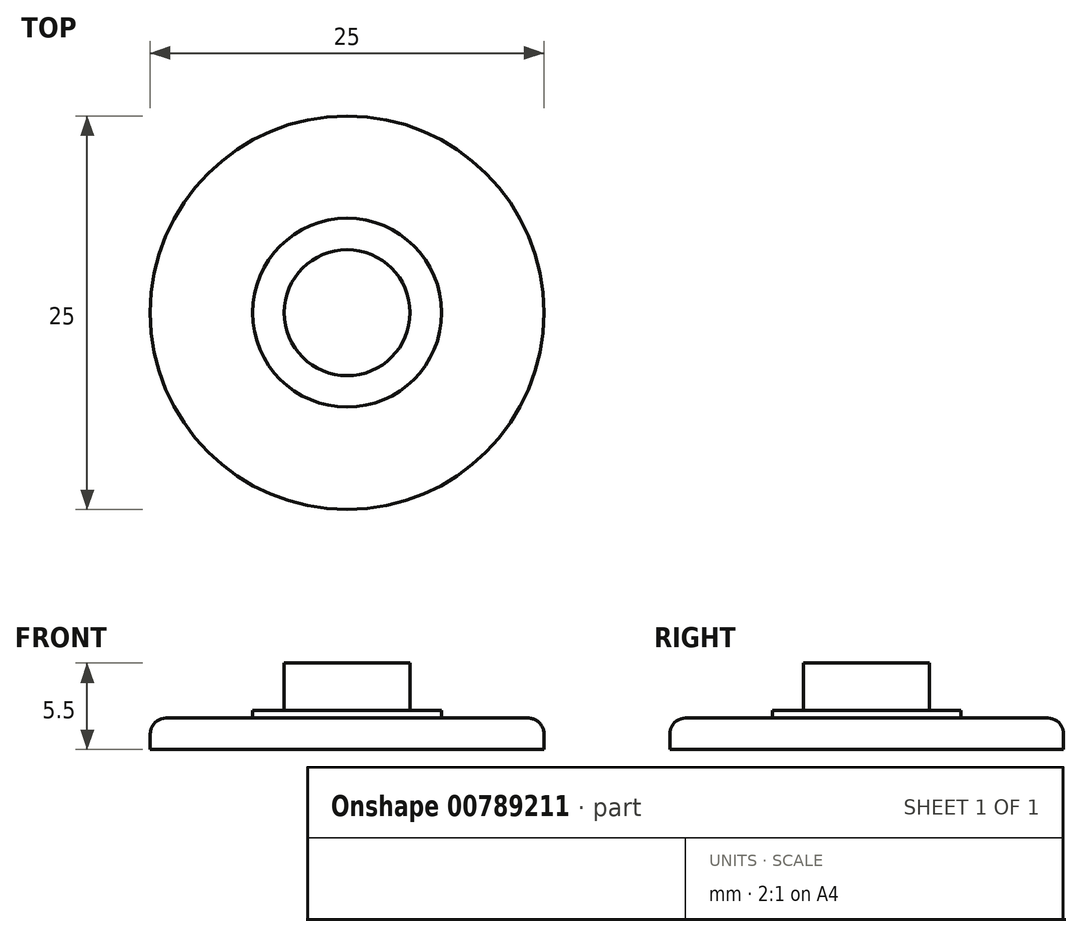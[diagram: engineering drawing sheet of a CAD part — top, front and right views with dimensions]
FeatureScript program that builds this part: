
annotation { "Feature Type Name" : "Feature", "Feature Type Description" : "" }
export const myFeature = defineFeature(function(context is Context, id is Id, definition is map)
    precondition{}
    {
        {
            var Q0;
            Q0=qCreatedBy(makeId("Top.planeOp"),FACE);
            var sketch = newSketch(context, id + "F0", { "sketchPlane" : qUnion([Q0])});
            skCircle(sketch, "E0", {"center": v(0, 0) * mm, "radius": 12.5 * mm});
            skSolve(sketch);
        }
        {
            var Q0;
            Q0 = qSketchRegion(id + "F0", true);
            extrude(context, id + "F1", {"entities" : qUnion([Q0]), "depth" : 2 * mm, "offsetDistance" : 25 * mm});
        }
        {
            var Q0;
            Q0=makeQuery(id+"F1.opExtrude","CAP_EDGE",EDGE,{"disambiguationData":[OSD([sQuery(id+"F0.wireOp",EDGE,"E0")])],"isStart":false});
            fillet(context, id + "F2", {"entities" : qUnion([Q0]), "radius" : 1 * mm, "tangentPropagation" : true, "allowEdgeOverflow" : false});
        }
        {
            var Q0;
            Q0=makeQuery(id+"F1.opExtrude","CAP_FACE",FACE,{"disambiguationData":[OSD([sQuery(id+"F0.wireOp",EDGE,"E0")])],"isStart":false});
            var sketch = newSketch(context, id + "F3", { "sketchPlane" : qUnion([Q0])});
            skCircle(sketch, "E1", {"center": v(0, 0) * mm, "radius": 6 * mm});
            skSolve(sketch);
        }
        {
            var Q0;
            Q0 = qSketchRegion(id + "F3", true);
            extrude(context, id + "F4", {"entities" : qUnion([Q0]), "operationType" : NewBodyOperationType.ADD, "depth" : 0.5 * mm, "offsetDistance" : 25 * mm});
        }
        {
            var Q0;
            Q0=makeQuery(id+"F4.opExtrude","CAP_FACE",FACE,{"disambiguationData":[OSD([sQuery(id+"F3.wireOp",EDGE,"E1")])],"isStart":false});
            var sketch = newSketch(context, id + "F5", { "sketchPlane" : qUnion([Q0])});
            skCircle(sketch, "E2", {"center": v(0, 0) * mm, "radius": 4 * mm});
            skSolve(sketch);
        }
        {
            var Q0;
            Q0=makeQuery(id+"F5.imprint","IMPRINT",FACE,{"disambiguationData":[TD([[makeQuery(id+"F5.imprint","IMPRINT",EDGE,{"derivedFrom":sQuery(id+"F5.wireOp",EDGE,"E2")}),1.0]])]});
            extrude(context, id + "F6", {"entities" : qUnion([Q0]), "operationType" : NewBodyOperationType.ADD, "depth" : 3 * mm, "offsetDistance" : 25 * mm});
        }
    });
